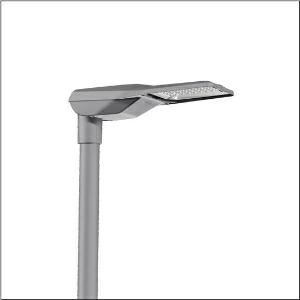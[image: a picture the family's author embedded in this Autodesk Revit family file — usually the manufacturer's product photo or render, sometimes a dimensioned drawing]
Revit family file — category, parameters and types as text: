
# Revit family: streetlight_sl_21_mini___st1_5a_5xe6p43a08gb_223e
name_source: partatom
category: Lighting Fixtures
units: mm (PartAtom-declared; Revit-internal decimal feet)

## family parameters
Cut with Voids When Loaded = No
Host = Face
Light Source = No
Part Type = Normal
Room Calculation Point = No
Round Connector Dimension = Use Diameter
Shared = No

## types (1)
- --- (1 x LED, 6080 lm, 40.4 W, 4000K)
    Apparent Load = 40 VA
    CIE Flux Codes = 22 53 95 100 100
    Color Rendering = 70
    Color Temperature = 4000K
    Default Elevation = 1800 mm
    Description = Streetlight SL 21 mini, mast luminaire, primary light control with lens, of PMMA, primary optical cover: cover, of toughened safety glass, transparent, light distribution: ST1.5a, light emission: direct distribution, primary light characteristic: asymmetric, installation type: post-top, side-entry, LED, 3G 1.5mm², High Power LED, rated luminous flux: 6.080lm, luminous efficacy: 151lm/W, light colour: 740, colour temperature: 4000K, control: overheat protection, constant luminous flux control, time-dependent luminous flux control, flexible luminous flux parameterisation, mains connection: 230..240V, AC, 50/60Hz, connection cable pre-assembled, cable length: 6,5m, wiring characteristics: H07RN-F, start of lifetime: 40W, end of service life: 41W, reduction: 19W, luminaire housing, of diecast aluminium, powder-coated, Siteco® metallic grey (DB 702S), corrosivity category C5 mid according to DIN EN ISO 12944, please order mast flange separately, inclination adjustable: 0°, 5°, 10°, 15°, sealing non-destructively replaceable, multi-level sealing system, length: 628mm, width: 235mm, height: 110mm, mast flange for spigot size: 42mm (side-entry): 5XC10008XM4, 60/48mm (side-entry/post-top): 5XC10108XM2, 76/60mm (side-entry/post-top): 5XC10108XM1, protection rating (complete): IP66, insulation class (complete): insulation class II (safety insulation), certification: CE, ENEC, ENEC+, VDE, impact resistance: IK09, permissible operating ambient temperature for outdoor applications: -40..+50°C, standard-compliant lighting for roads and squares, packaging unit: 1 piece

Light Distribution: ST1.5a
    Height = 110 mm
    Lamp = 1 x LED
    Lamp Light Flux = 6080 lm
    Lamp Power = 40.4 W
    Lamp count = 1
    Length = 625 mm
    Luminous efficacy = 151 lm/W
    Manufacturer = Siteco
    ModVariant = No
    Model = 5XE6P43A08GB
    Number of Poles = 1
    OnlyDefault = Yes
    Power Factor = 1
    Product Name = Streetlight SL 21 mini | ST1.5a
    Product group = mast luminaire | pylon top
    ProductGroupID = 6100
    Protection Class = Protection class II
    Protection Degree = IP 66
    RLX_Detail_Level = 1
    RLX_Emergency_Light_Flux = 0 lm
    RLX_Emergency_Type = 0
    RLX_Emergency_Type_DB = No
    RlxData = <blob elided: 96877 chars, md5=29243f25>
    Socket = socket
    Standby Power = 0 W
    System Light Flux = 6080 lm
    System Power = 40 W
    Type Comments = factory setting: luminous flux: 100 % | Output Level: 100 % | 812 mA
    Type Image = l_1003519.jpg
    URL = http://relux.com
    VarID = @adj_126395
    Voltage = 0 V
    Weight = 0.00 kg
    Width = 234 mm

## geometry (parser evidence)
native form markers: Blend x4, Sweep x9
no freeform markers — native parametric forms only
